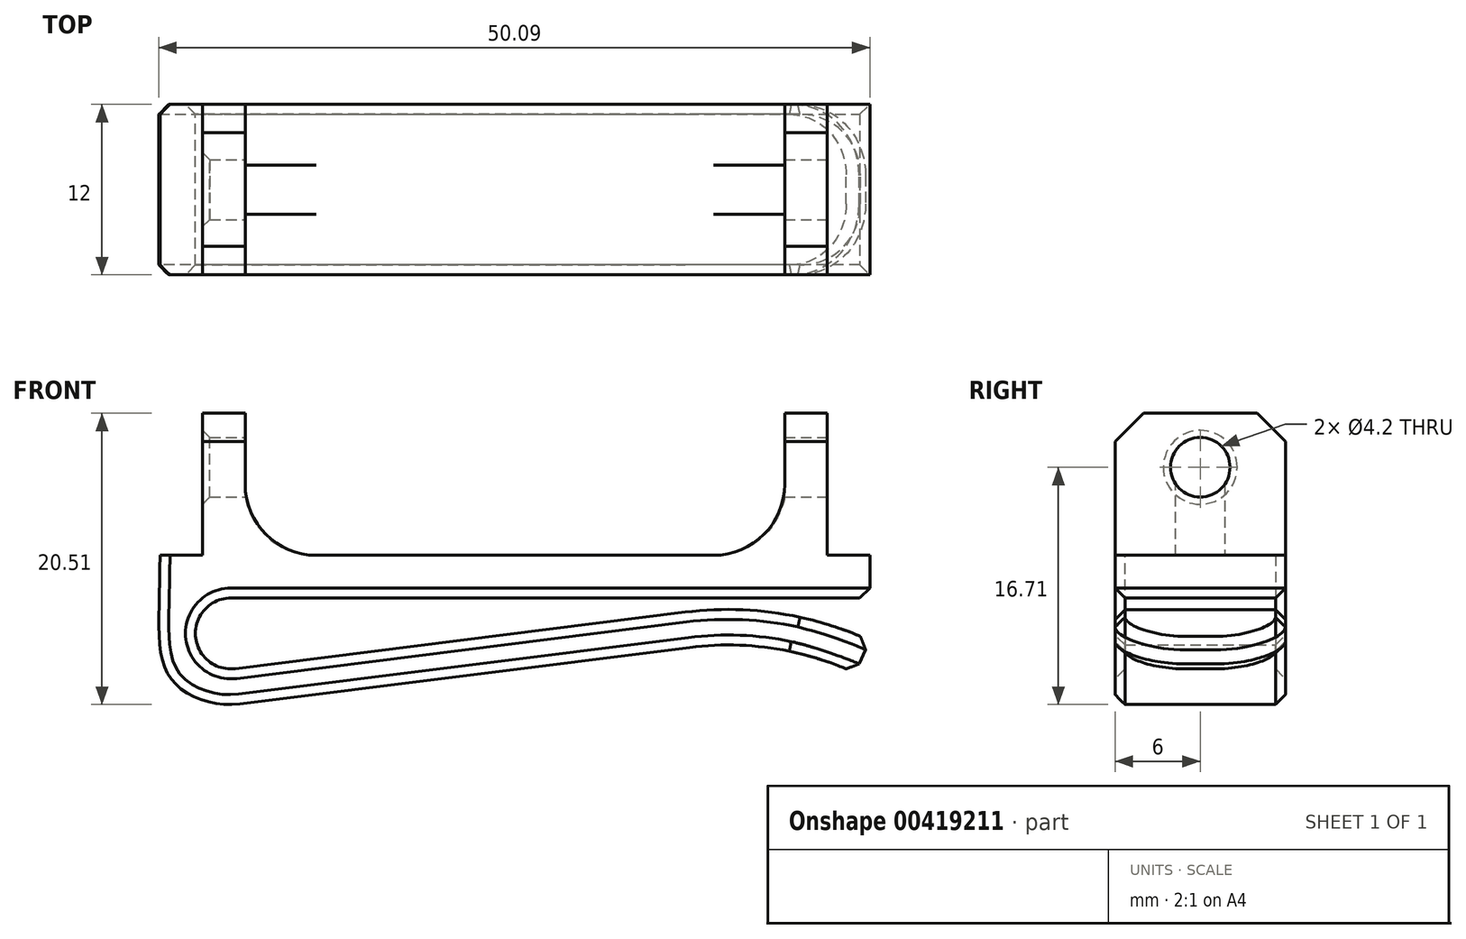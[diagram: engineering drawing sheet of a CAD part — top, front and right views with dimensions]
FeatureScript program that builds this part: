
annotation { "Feature Type Name" : "Feature", "Feature Type Description" : "" }
export const myFeature = defineFeature(function(context is Context, id is Id, definition is map)
    precondition{}
    {
        {
            var Q0;
            Q0=qCreatedBy(makeId("Front.planeOp"),FACE);
            var sketch = newSketch(context, id + "F0", { "sketchPlane" : qUnion([Q0])});
            skLineSegment(sketch, "E0", {"start": v(5, -3) * mm, "end": v(50, -3) * mm});
            skArc(sketch, "E1", {"start": v(5, -3) * mm, "mid": v(2.5, -5.66) * mm, "end": v(5.3, -7.98) * mm});
            skLineSegment(sketch, "E2", {"start": v(5.3, -7.98) * mm, "end": v(37, -4) * mm});
            skArc(sketch, "E3", {"start": v(50, -6) * mm, "mid": v(43.64, -4.1) * mm, "end": v(37, -4) * mm});
            skPoint(sketch, "E4", {"position": v(42.98, -4) * mm});
            skLineSegment(sketch, "E5", {"start": v(42.98, -4) * mm, "end": v(53.63, -4) * mm, "construction": true});
            skLineSegment(sketch, "E6", {"start": v(2.5, -1.32) * mm, "end": v(2.5, -12.17) * mm, "construction": true});
            skPoint(sketch, "E6.startSnap0", {"position": v(2.5, -5.66) * mm});
            skLineSegment(sketch, "E7", {"start": v(50, -3) * mm, "end": v(50, 0) * mm});
            skLineSegment(sketch, "E8", {"start": v(50, 0) * mm, "end": v(0, 0) * mm});
            skArc(sketch, "E9.0", {"start": v(48.96, -8.27) * mm, "mid": v(43.26, -6.56) * mm, "end": v(37.31, -6.48) * mm});
            skLineSegment(sketch, "E10.0", {"start": v(5.62, -10.46) * mm, "end": v(37.31, -6.48) * mm});
            skLineSegment(sketch, "E11", {"start": v(48.96, -8.27) * mm, "end": v(50, -6) * mm});
            skLineSegment(sketch, "E12", {"start": v(0, 0) * mm, "end": v(0, 10.86) * mm, "construction": true});
            skLineSegment(sketch, "E13", {"start": v(5.3, -7.98) * mm, "end": v(5.62, -10.46) * mm, "construction": true});
            skFitSpline(sketch, "E14", {"points": [v(0, 0) * mm, v(0.8, -8.72) * mm, v(5.62, -10.46) * mm], "startDerivative": vector(0, -22.7) * mm, "endDerivative": vector(12.77, 1.6) * mm});
            skSolve(sketch);
        }
        {
            var Q0;
            Q0 = qSketchRegion(id + "F0", true);
            extrude(context, id + "F1", {"entities" : qUnion([Q0]), "endBound" : BoundingType.SYMMETRIC, "depth" : 12 * mm});
        }
        {
            var Q0;
            Q0=makeQuery(id+"F1.opExtrude","CAP_FACE",FACE,{"disambiguationData":[OSD([sQuery(id+"F0.wireOp",EDGE,"E0"),sQuery(id+"F0.wireOp",EDGE,"E1"),sQuery(id+"F0.wireOp",EDGE,"E2"),sQuery(id+"F0.wireOp",EDGE,"E3"),sQuery(id+"F0.wireOp",EDGE,"E7"),sQuery(id+"F0.wireOp",EDGE,"E8"),sQuery(id+"F0.wireOp",EDGE,"E9.0"),sQuery(id+"F0.wireOp",EDGE,"E10.0"),sQuery(id+"F0.wireOp",EDGE,"E11"),sQuery(id+"F0.wireOp",EDGE,"E14")])],"isStart":false});
            var sketch = newSketch(context, id + "F2", { "sketchPlane" : qUnion([Q0])});
            skLineSegment(sketch, "E15.bottom", {"start": v(3, 0) * mm, "end": v(6, 0) * mm});
            skLineSegment(sketch, "E15.top", {"start": v(3, 10) * mm, "end": v(6, 10) * mm});
            skLineSegment(sketch, "E15.left", {"start": v(3, 0) * mm, "end": v(3, 10) * mm});
            skLineSegment(sketch, "E15.right", {"start": v(6, 0) * mm, "end": v(6, 10) * mm});
            skLineSegment(sketch, "E16.bottom", {"start": v(47, 0) * mm, "end": v(44, 0) * mm});
            skLineSegment(sketch, "E16.top", {"start": v(47, 10) * mm, "end": v(44, 10) * mm});
            skLineSegment(sketch, "E16.left", {"start": v(47, 0) * mm, "end": v(47, 10) * mm});
            skLineSegment(sketch, "E16.right", {"start": v(44, 0) * mm, "end": v(44, 10) * mm});
            skSolve(sketch);
        }
        {
            var Q0;
            Q0 = qSketchRegion(id + "F2", true);
            var Q1;
            Q1=makeQuery(id+"F1.opExtrude","CAP_FACE",FACE,{"disambiguationData":[OSD([sQuery(id+"F0.wireOp",EDGE,"E0"),sQuery(id+"F0.wireOp",EDGE,"E1"),sQuery(id+"F0.wireOp",EDGE,"E2"),sQuery(id+"F0.wireOp",EDGE,"E3"),sQuery(id+"F0.wireOp",EDGE,"E7"),sQuery(id+"F0.wireOp",EDGE,"E8"),sQuery(id+"F0.wireOp",EDGE,"E9.0"),sQuery(id+"F0.wireOp",EDGE,"E10.0"),sQuery(id+"F0.wireOp",EDGE,"E11"),sQuery(id+"F0.wireOp",EDGE,"E14")])],"isStart":true});
            extrude(context, id + "F3", {"entities" : qUnion([Q0]), "operationType" : NewBodyOperationType.ADD, "endBound" : BoundingType.UP_TO_SURFACE, "oppositeDirection" : true, "endBoundEntityFace" : qUnion([Q1]), "depth" : 25 * mm});
        }
        {
            var Q0;
            Q0=makeQuery(id+"F3.opExtrude","SWEPT_FACE",FACE,{"disambiguationData":[OSD([sQuery(id+"F2.wireOp",EDGE,"E16.left")])]});
            var sketch = newSketch(context, id + "F4", { "sketchPlane" : qUnion([Q0])});
            skCircle(sketch, "E17", {"center": v(0, 6.2) * mm, "radius": 2.1 * mm});
            skSolve(sketch);
        }
        {
            var Q0;
            Q0 = qSketchRegion(id + "F4", true);
            extrude(context, id + "F5", {"entities" : qUnion([Q0]), "operationType" : NewBodyOperationType.REMOVE, "endBound" : BoundingType.THROUGH_ALL, "oppositeDirection" : true, "depth" : 25 * mm});
        }
        {
            var Q0;
            Q0=makeQuery(id+"F5.boolean.opBoolean","INTERSECT",EDGE,{"derivedFrom":[makeQuery(id+"F3.opExtrude","SWEPT_FACE",FACE,{"disambiguationData":[OSD([sQuery(id+"F2.wireOp",EDGE,"E15.left")])]}),makeQuery(id+"F5.opExtrude","SWEPT_FACE",FACE,{"disambiguationData":[OSD([sQuery(id+"F4.wireOp",EDGE,"E17")])]})]});
            var Q1;
            Q1=makeQuery(id+"F5.boolean.opBoolean","COPY",EDGE,{"derivedFrom":makeQuery(id+"F5.opExtrude","CAP_EDGE",EDGE,{"disambiguationData":[OSD([sQuery(id+"F4.wireOp",EDGE,"E17")])],"isStart":true})});
            chamfer(context, id + "F6", {"entities" : qUnion([Q0, Q1]), "width" : .5 * mm, "tangentPropagation" : true});
        }
        {
            var Q0;
            Q0=makeQuery(id+"F3.opExtrude","SWEPT_EDGE",EDGE,{"disambiguationData":[OSD([sQuery(id+"F0.wireOp",EDGE,"E8"),sQuery(id+"F2.wireOp",EDGE,"E15.bottom"),sQuery(id+"F2.wireOp",EDGE,"E15.right")])]});
            var Q1;
            Q1=makeQuery(id+"F3.opExtrude","SWEPT_EDGE",EDGE,{"disambiguationData":[OSD([sQuery(id+"F0.wireOp",EDGE,"E8"),sQuery(id+"F2.wireOp",EDGE,"E16.bottom"),sQuery(id+"F2.wireOp",EDGE,"E16.right")])]});
            fillet(context, id + "F7", {"entities" : qUnion([Q0, Q1]), "radius" : 5 * mm, "tangentPropagation" : true, "allowEdgeOverflow" : false});
        }
        {
            var Q0;
            Q0=makeQuery(id+"F3.opExtrude","CAP_EDGE",EDGE,{"disambiguationData":[OSD([sQuery(id+"F2.wireOp",EDGE,"E15.top")])],"isStart":false});
            var Q1;
            Q1=makeQuery(id+"F3.opExtrude","CAP_EDGE",EDGE,{"disambiguationData":[OSD([sQuery(id+"F2.wireOp",EDGE,"E15.top")])],"isStart":true});
            var Q2;
            Q2=makeQuery(id+"F3.opExtrude","CAP_EDGE",EDGE,{"disambiguationData":[OSD([sQuery(id+"F2.wireOp",EDGE,"E16.top")])],"isStart":false});
            var Q3;
            Q3=makeQuery(id+"F3.opExtrude","CAP_EDGE",EDGE,{"disambiguationData":[OSD([sQuery(id+"F2.wireOp",EDGE,"E16.top")])],"isStart":true});
            chamfer(context, id + "F8", {"entities" : qUnion([Q0, Q1, Q2, Q3]), "width" : 2 * mm, "tangentPropagation" : true});
        }
        {
            var Q0;
            Q0=makeQuery(id+"F1.opExtrude","CAP_EDGE",EDGE,{"disambiguationData":[OSD([sQuery(id+"F0.wireOp",EDGE,"E11")])],"isStart":false});
            var Q1;
            Q1=makeQuery(id+"F1.opExtrude","CAP_EDGE",EDGE,{"disambiguationData":[OSD([sQuery(id+"F0.wireOp",EDGE,"E11")])],"isStart":true});
            fillet(context, id + "F9", {"entities" : qUnion([Q0, Q1]), "radius" : 5 * mm, "tangentPropagation" : true, "allowEdgeOverflow" : false});
        }
        {
            var Q0;
            Q0=makeQuery(id+"F1.opExtrude","CAP_EDGE",EDGE,{"disambiguationData":[OSD([sQuery(id+"F0.wireOp",EDGE,"E10.0")])],"isStart":true});
            chamfer(context, id + "F10", {"entities" : qUnion([Q0]), "width" : 0.7 * mm, "tangentPropagation" : true});
        }
        {
            var Q0;
            Q0=makeQuery(id+"F9.opFillet","BLEND_EDGE",EDGE,{"blendedFrom":[makeQuery(id+"F1.opExtrude","CAP_EDGE",EDGE,{"disambiguationData":[OSD([sQuery(id+"F0.wireOp",EDGE,"E11")])],"isStart":true}),makeQuery(id+"F1.opExtrude","SWEPT_FACE",FACE,{"disambiguationData":[OSD([sQuery(id+"F0.wireOp",EDGE,"E3")])]})],"blendedInto":[makeQuery(id+"F1.opExtrude","SWEPT_FACE",FACE,{"disambiguationData":[OSD([sQuery(id+"F0.wireOp",EDGE,"E3")])]})]});
            var Q1;
            Q1=makeQuery(id+"F1.opExtrude","SWEPT_EDGE",EDGE,{"disambiguationData":[OSD([sQuery(id+"F0.wireOp",EDGE,"E0"),sQuery(id+"F0.wireOp",EDGE,"E7")])]});
            chamfer(context, id + "F11", {"entities" : qUnion([Q0, Q1]), "width" : 0.7 * mm, "tangentPropagation" : true});
        }
    });
